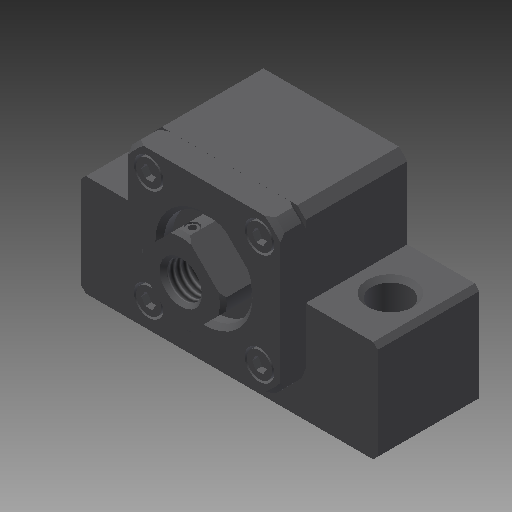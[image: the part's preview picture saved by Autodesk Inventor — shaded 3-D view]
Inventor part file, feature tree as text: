
AUTODESK INVENTOR PART (.ipt)
format: ipt  version: 2018 (Build 220112000, 112)  size: 373,248 bytes
history: native  units: mm
features: sketch x23, revolve x14, other x14, extrude x8, pattern_linear x3, thread x1, hole x1
ambient origin geometry x8: Origin, YZ Plane, XZ Plane, XY Plane, X Axis, Y Axis, Z Axis, Center Point
bodies: Solid1 (feature_tree)
feature tree (64):
  extrude  "Extrusion1"  TaperAngle=360.0deg  [1 undecoded]
  revolve  "Revolution1"  [1 undecoded]
  revolve  "Revolution2"  [1 undecoded]
  extrude  "Extrusion2"  TaperAngle=360.0deg  [1 undecoded]
  revolve  "Revolution3"  [1 undecoded]
  extrude  "Extrusion3"  TaperAngle=360.0deg  [1 undecoded]
  extrude  "Extrusion4"  Depth=20.0mm
  revolve  "Revolution4"  [1 undecoded]
  revolve  "Revolution5"  Angle=360.0deg
  thread  "Thread1"  [1 undecoded]
  revolve  "Revolution6"  [1 undecoded]
  revolve  "Revolution7"  Angle=360.0deg
  extrude  "Extrusion5"  TaperAngle=360.0deg  [1 undecoded]
  pattern_linear  "Rectangular Pattern1"  [2 undecoded]
  pattern_linear  "Rectangular Pattern2"  [2 undecoded]
  pattern_linear  "Rectangular Pattern3"  [2 undecoded]
  revolve  "Revolution8"  [1 undecoded]
  revolve  "Revolution9"  [1 undecoded]
  revolve  "Revolution10"  [1 undecoded]
  revolve  "Revolution11"  [1 undecoded]
  extrude  "Extrusion6"  [1 undecoded]
  hole  "Hole1"  [1 undecoded]
  revolve  "Revolution12"  [1 undecoded]
  extrude  "Extrusion7"  [1 undecoded]
  revolve  "Revolution13"  [1 undecoded]
  revolve  "Revolution14"  [1 undecoded]
  extrude  "Extrusion8"  [1 undecoded]
  other  "unit_XY"
  other  "unit_YZ"
  other  "unit_ZX"
  other  "unit_X"
  other  "unit_Y"
  other  "unit_Z"
  other  "unit_Center"
  other  "unit_collar_XY"
  other  "unit_collar_YZ"
  other  "unit_collar_ZX"
  other  "unit_collar_X"
  other  "unit_collar_Y"
  other  "unit_collar_Z"
  other  "unit_collar_Center"
  sketch  "Sketch_1"  dims[d0=24.0mm d1=0.0mm d2=360.0deg]
  sketch  "Sketch_3"  dims[d3=360.0deg d4=3.0mm d5=0.0mm]
  sketch  "Sketch_4"  dims[d6=360.0deg d7=8.5mm d8=0.0mm]
  sketch  "Sketch_17"  dims[d12=360.0deg d13=6.376mm d14=0.0mm]
  sketch  "Sketch_19"  dims[d25=20.0mm d27=26.162951mm d28=20.0mm d30=26.162951mm d31=20.0mm d33=26.162951mm d34=20.0mm d36=26.162951mm]
  sketch  "Sketch_18"  dims[d15=360.0deg d16=360.0deg]
  sketch  "Sketch_20"  dims[d37=360.0deg d38=360.0deg d39=360.0deg]
  sketch  "Sketch_21"  dims[d40=360.0deg d41=1.2mm d42=0.0mm]
  sketch  "Sketch_22"  dims[d43=10.0mm d44=6.0mm d45=14.5mm d46=6.0mm d47=90.0deg d48=27.5mm d49=0.0mm d50=360.0deg]
  sketch  "Sketch_24"  dims[d51=6.0mm d52=0.0mm d53=360.0deg]
  sketch  "Sketch_25"  dims[d54=360.0deg]
  sketch  "Sketch_28"  dims[d55=0.01mm d56=0.0mm]
  sketch  "Sketch_30"  dims[d57=0.0mm d58=0.0mm]
  sketch  "Sketch_31"
  sketch  "Sketch_32"
  sketch  "Sketch_33"
  sketch  "Sketch_34"
  sketch  "Sketch18"  dims[d17=3.0mm d18=0.0mm d19=20.0mm d21=26.162951mm d22=20.0mm d24=26.162951mm]
  sketch  "Sketch_55"
  sketch  "Sketch_16"  dims[d9=3.0mm d10=0.0mm d11=360.0deg]
  sketch  "Sketch_35"
  sketch  "Sketch_50"
  sketch  "Sketch_51"
note: 27 required parameter values undecoded (feature->parameter linkage not recoverable at this tier; creation-order binding heuristic only, values carry confidence <= 0.55)